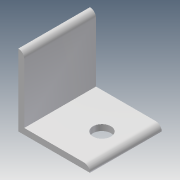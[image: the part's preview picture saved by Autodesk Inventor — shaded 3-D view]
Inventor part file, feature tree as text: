
AUTODESK INVENTOR PART (.ipt)
format: ipt  version: 2014 (Build 180170000, 170)  size: 89,088 bytes
history: native  units: in
note: dims shown in document units (in); Inventor stores cm internally (conversion verified against a paired STEP export)
features: extrude x2, sketch x2
ambient origin geometry x8: Origin, YZ Plane, XZ Plane, XY Plane, X Axis, Y Axis, Z Axis, Center Point
bodies: Solid1 (feature_tree)
feature tree (4):
  extrude  "Extrusion1"  Depth=1.5in
  extrude  "Extrusion2"  Depth=1.5in TaperAngle=0.0deg
  sketch  "Sketch1"  dims[d0=1.5in d1=1.5in]
  sketch  "Sketch2"  dims[d2=0.125in d3=1.5in d4=0.0in d5=0.375in d6=0.5in d7=1.5in d8=0.0in]
